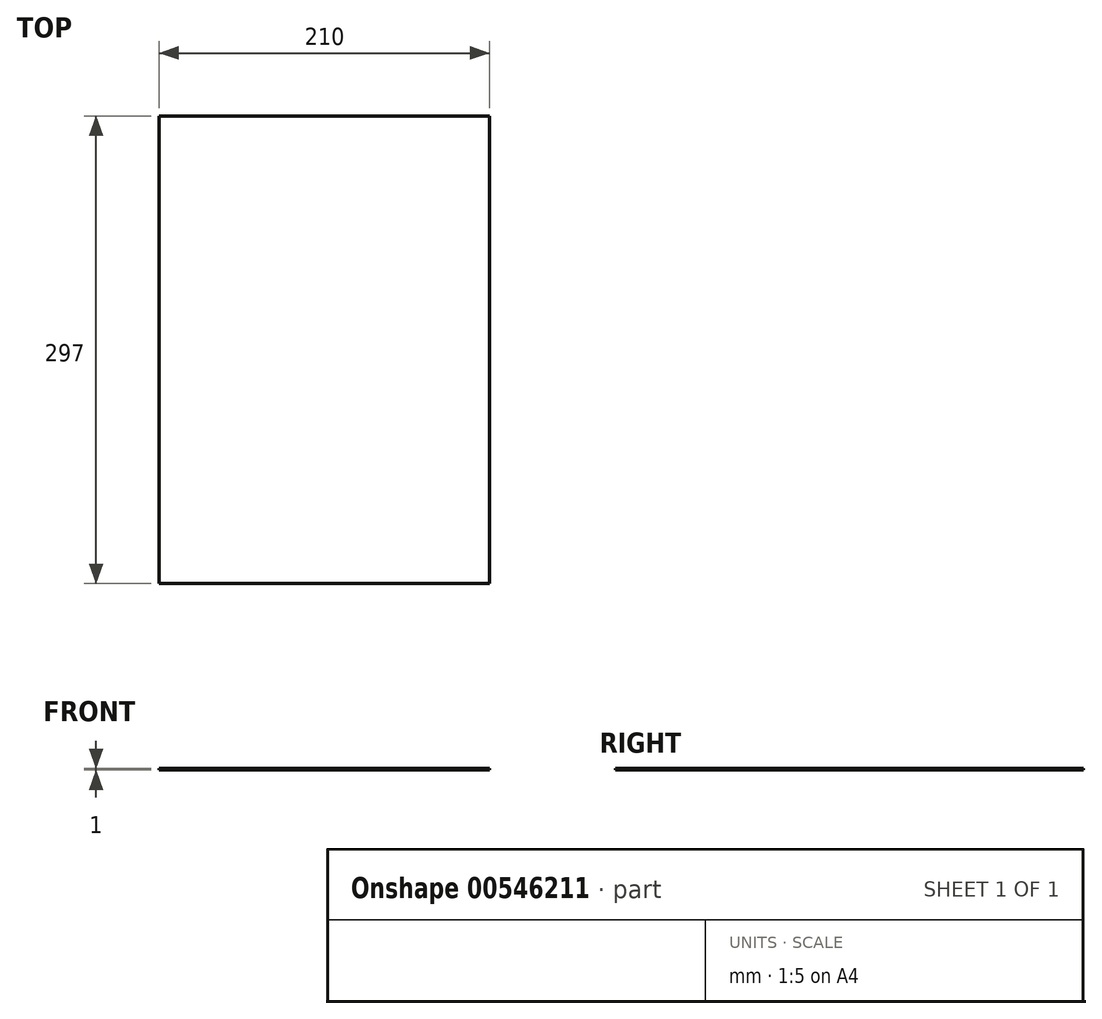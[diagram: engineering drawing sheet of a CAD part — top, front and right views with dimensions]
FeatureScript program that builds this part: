
annotation { "Feature Type Name" : "Feature", "Feature Type Description" : "" }
export const myFeature = defineFeature(function(context is Context, id is Id, definition is map)
    precondition{}
    {
        {
            var Q0;
            Q0=qCreatedBy(makeId("Top.planeOp"),FACE);
            var sketch = newSketch(context, id + "F0", { "sketchPlane" : qUnion([Q0])});
            skLineSegment(sketch, "E0.bottom", {"start": v(-210, 148.5) * mm, "end": v(0, 148.5) * mm});
            skLineSegment(sketch, "E0.top", {"start": v(-210, -148.5) * mm, "end": v(0, -148.5) * mm});
            skLineSegment(sketch, "E0.left", {"start": v(-210, 148.5) * mm, "end": v(-210, -148.5) * mm});
            skLineSegment(sketch, "E0.right", {"start": v(0, 148.5) * mm, "end": v(0, -148.5) * mm});
            skSolve(sketch);
        }
        {
            var Q0;
            Q0=makeQuery(id+"F0.imprint","IMPRINT",FACE,{"disambiguationData":[TD([[makeQuery(id+"F0.imprint","IMPRINT",EDGE,{"derivedFrom":sQuery(id+"F0.wireOp",EDGE,"E0.bottom")}),-1.0]])]});
            extrude(context, id + "F1", {"entities" : qUnion([Q0]), "depth" : 0.5 * mm, "offsetDistance" : 25.4 * mm});
        }
        {
            var Q0;
            Q0=makeQuery(id+"F1.opExtrude","SWEPT_BODY",BODY,{"disambiguationData":[OSD([sQuery(id+"F0.wireOp",EDGE,"E0.bottom"),sQuery(id+"F0.wireOp",EDGE,"E0.top"),sQuery(id+"F0.wireOp",EDGE,"E0.left"),sQuery(id+"F0.wireOp",EDGE,"E0.right")])]});
            var Q1;
            Q1=qCreatedBy(makeId("Top.planeOp"),FACE);
            mirror(context, id + "F2", {"operationType" : NewBodyOperationType.ADD, "entities" : qUnion([Q0]), "mirrorPlane" : qUnion([Q1])});
        }
    });
